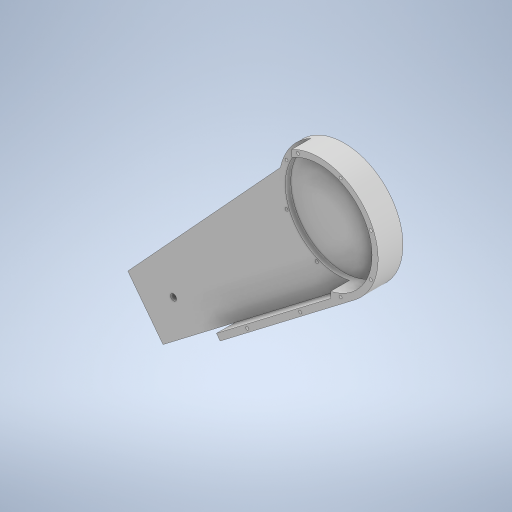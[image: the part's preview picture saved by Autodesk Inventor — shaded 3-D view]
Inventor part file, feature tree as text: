
AUTODESK INVENTOR PART (.ipt)
format: ipt  version: 2024.3 (Build 283343000, 343)  size: 405,504 bytes
history: native  units: mm
features: sketch x11, extrude x8, hole x3, other x1
ambient origin geometry x8: Origin, YZ Plane, XZ Plane, XY Plane, X Axis, Y Axis, Z Axis, Center Point
bodies: Body1 (feature_tree)
feature tree (23):
  other  "ソリッド1"
  extrude  "押し出し1"  Depth=97.0mm
  hole  "穴1"  [1 undecoded]
  extrude  "押し出し2"  Depth=20.5mm TaperAngle=0.0deg
  extrude  "押し出し3"  Depth=92.0mm
  extrude  "押し出し4"  TaperAngle=22.5deg  [1 undecoded]
  hole  "穴2"  [1 undecoded]
  hole  "穴3"  [1 undecoded]
  extrude  "押し出し5"  Depth=20.0mm TaperAngle=0.0deg
  extrude  "押し出し6"  Depth=48.5mm
  extrude  "押し出し7"  Depth=97.0mm
  extrude  "押し出し8"  Depth=220.0mm
  sketch  "スケッチ1"
  sketch  "スケッチ2"
  sketch  "スケッチ3"
  sketch  "スケッチ4"
  sketch  "スケッチ5"
  sketch  "スケッチ6"
  sketch  "スケッチ7"
  sketch  "スケッチ8"
  sketch  "スケッチ9"
  sketch  "スケッチ10"
  sketch  "スケッチ11"
note: 4 required parameter values undecoded (feature->parameter linkage not recoverable at this tier; creation-order binding heuristic only, values carry confidence <= 0.55)
